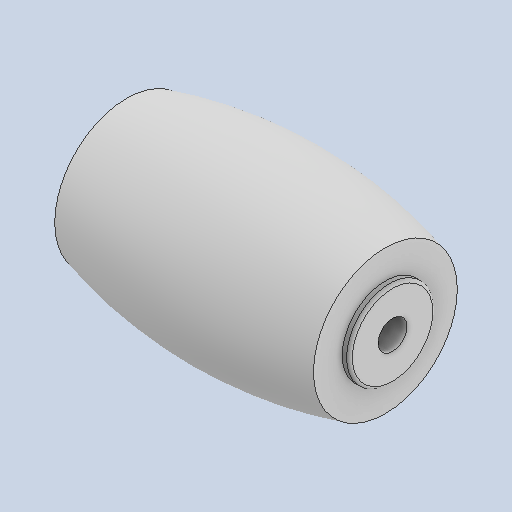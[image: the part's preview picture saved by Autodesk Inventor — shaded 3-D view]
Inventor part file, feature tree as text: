
AUTODESK INVENTOR PART (.ipt)
format: ipt  version: 2023 (Build 270158000, 158)  size: 120,320 bytes
history: native  units: mm
features: fillet x1
ambient origin geometry x8: Origin, YZ Plane, XZ Plane, XY Plane, X Axis, Y Axis, Z Axis, Center Point
bodies: Solid1 (feature_tree)
feature tree (1):
  fillet  "Fillet1"  [1 undecoded]
note: 1 required parameter value undecoded (feature->parameter linkage not recoverable at this tier; creation-order binding heuristic only, values carry confidence <= 0.55)
